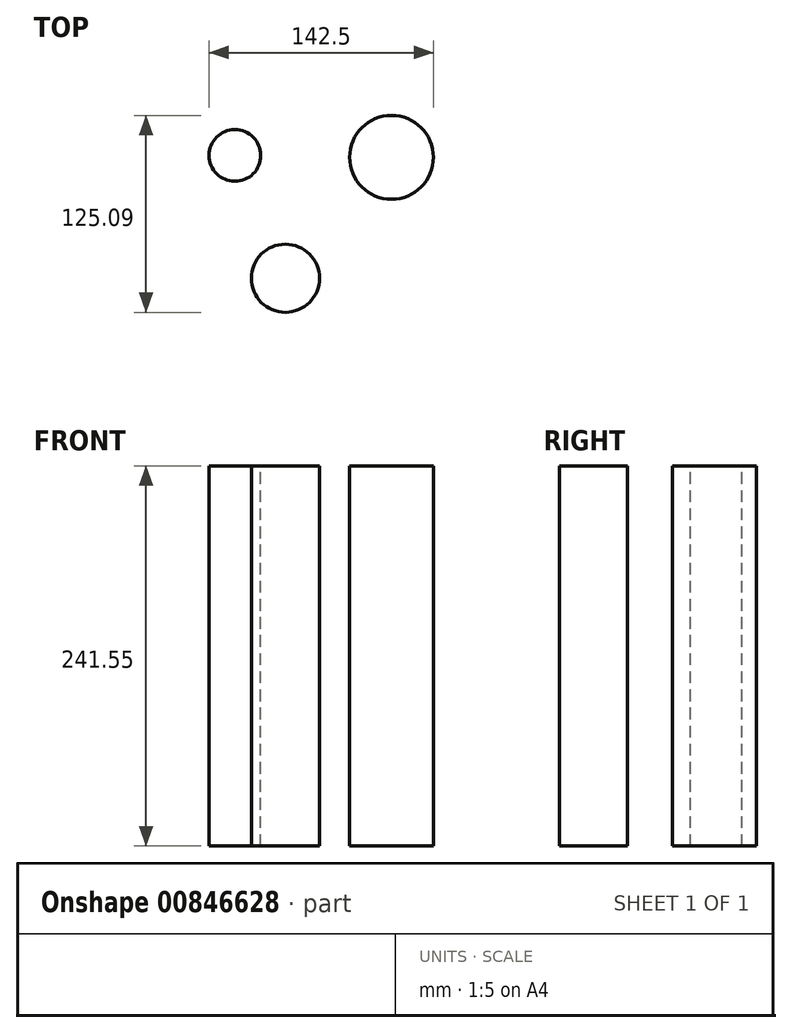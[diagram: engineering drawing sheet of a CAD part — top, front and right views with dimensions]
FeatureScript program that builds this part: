
annotation { "Feature Type Name" : "Feature", "Feature Type Description" : "" }
export const myFeature = defineFeature(function(context is Context, id is Id, definition is map)
    precondition{}
    {
        {
            var Q0;
            Q0=qCreatedBy(makeId("Top.planeOp"),FACE);
            var sketch = newSketch(context, id + "F0", { "sketchPlane" : qUnion([Q0])});
            skCircle(sketch, "E0", {"center": v(-67.36, 51.17) * mm, "radius": 16.4 * mm});
            skCircle(sketch, "E1", {"center": v(32.11, 49.98) * mm, "radius": 26.62 * mm});
            skCircle(sketch, "E2", {"center": v(-35.3, -26.83) * mm, "radius": 21.65 * mm});
            skLineSegment(sketch, "E3", {"start": v(-70.1, -59.76) * mm, "end": v(-111.63, 80.4) * mm});
            skLineSegment(sketch, "E4", {"start": v(-112.47, 80.1) * mm, "end": v(59, 95.15) * mm});
            skLineSegment(sketch, "E5", {"start": v(59, 95.15) * mm, "end": v(92.17, 33.25) * mm});
            skLineSegment(sketch, "E6", {"start": v(92.17, 33.25) * mm, "end": v(-18.93, 13.37) * mm});
            skLineSegment(sketch, "E7", {"start": v(-18.93, 13.37) * mm, "end": v(18.16, -24.67) * mm});
            skLineSegment(sketch, "E8", {"start": v(17.1, -25.62) * mm, "end": v(0, -68.13) * mm});
            skLineSegment(sketch, "E9", {"start": v(1.27, -67.3) * mm, "end": v(18.16, -84) * mm});
            skLineSegment(sketch, "E10", {"start": v(18.16, -84) * mm, "end": v(-37.77, -68.13) * mm});
            skLineSegment(sketch, "E11", {"start": v(-37.95, -64.26) * mm, "end": v(-52.47, -90.32) * mm});
            skLineSegment(sketch, "E12", {"start": v(-52.66, -89.83) * mm, "end": v(-52.25, -56.26) * mm});
            skLineSegment(sketch, "E13", {"start": v(-52.25, -56.26) * mm, "end": v(-70.1, -59.76) * mm});
            skSolve(sketch);
        }
        {
            var Q0;
            Q0=makeQuery(id+"F0.imprint","IMPRINT",FACE,{"disambiguationData":[TD([[makeQuery(id+"F0.imprint","IMPRINT",EDGE,{"derivedFrom":sQuery(id+"F0.wireOp",EDGE,"E0")}),1.0]])]});
            var Q1;
            Q1=makeQuery(id+"F0.imprint","IMPRINT",FACE,{"disambiguationData":[TD([[makeQuery(id+"F0.imprint","IMPRINT",EDGE,{"derivedFrom":sQuery(id+"F0.wireOp",EDGE,"E1")}),1.0]])]});
            var Q2;
            Q2=makeQuery(id+"F0.imprint","IMPRINT",FACE,{"disambiguationData":[TD([[makeQuery(id+"F0.imprint","IMPRINT",EDGE,{"derivedFrom":sQuery(id+"F0.wireOp",EDGE,"E2")}),1.0]])]});
            extrude(context, id + "F1", {"entities" : qUnion([Q0, Q1, Q2]), "oppositeDirection" : true, "depth" : 241.55 * mm, "offsetDistance" : 25.4 * mm});
        }
    });
